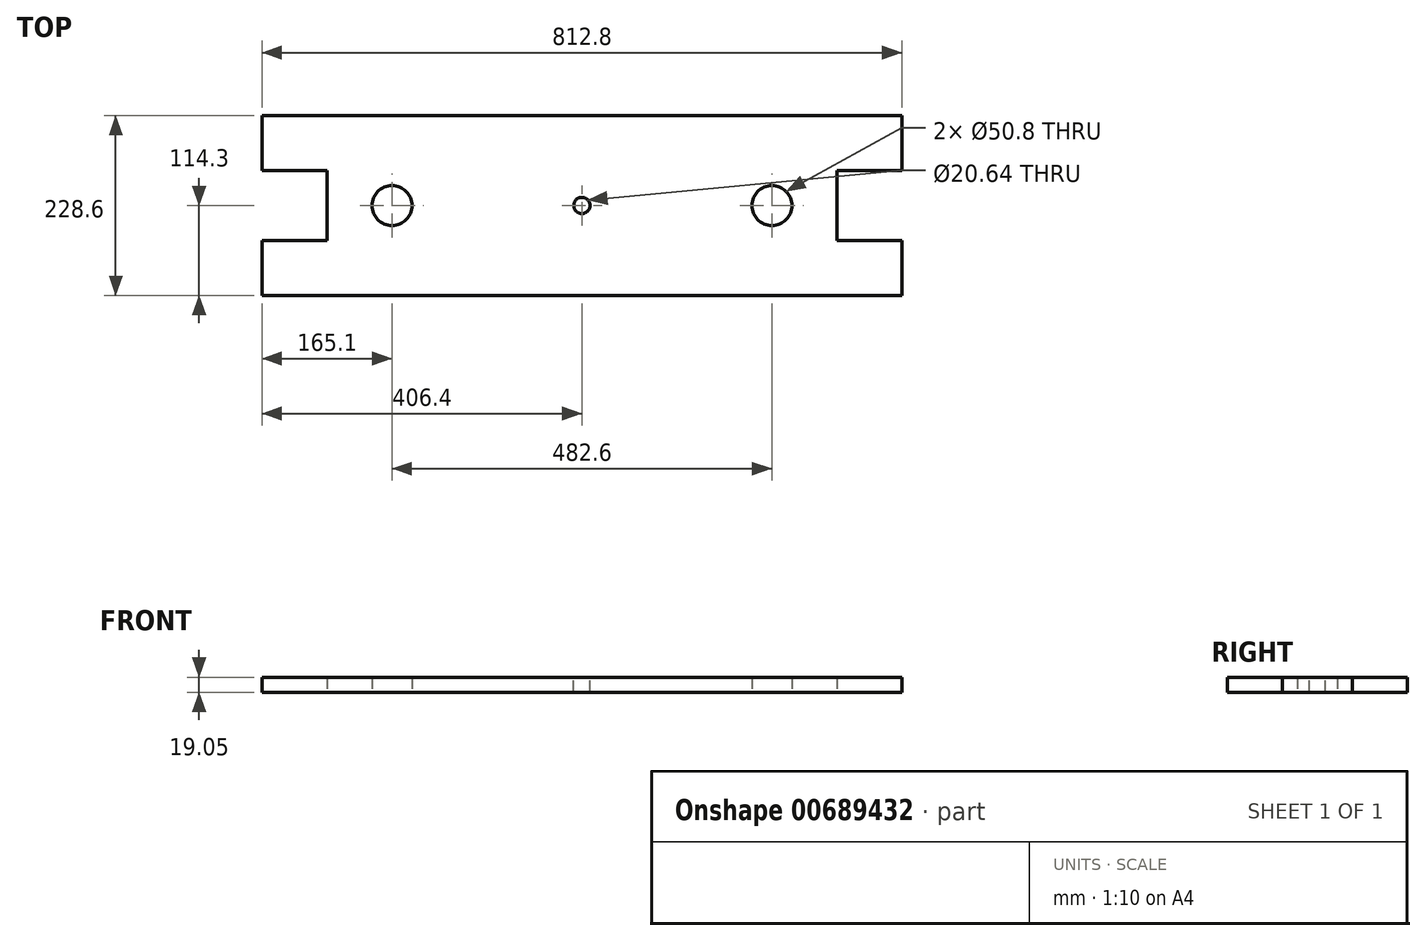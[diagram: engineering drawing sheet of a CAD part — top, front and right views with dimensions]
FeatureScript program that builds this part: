
annotation { "Feature Type Name" : "Feature", "Feature Type Description" : "" }
export const myFeature = defineFeature(function(context is Context, id is Id, definition is map)
    precondition{}
    {
        {
            var Q0;
            Q0=qCreatedBy(makeId("Top.planeOp"),FACE);
            var sketch = newSketch(context, id + "F0", { "sketchPlane" : qUnion([Q0])});
            skLineSegment(sketch, "E0.bottom", {"start": v(-406.4, 114.3) * mm, "end": v(406.4, 114.3) * mm});
            skLineSegment(sketch, "E0.top", {"start": v(-406.4, -114.3) * mm, "end": v(406.4, -114.3) * mm});
            skLineSegment(sketch, "E0.left", {"start": v(-406.4, 114.3) * mm, "end": v(-406.4, 44.45) * mm});
            skLineSegment(sketch, "E0.right", {"start": v(406.4, 114.3) * mm, "end": v(406.4, 44.45) * mm});
            skPoint(sketch, "E0.middle", {"position": v(365.13, 0) * mm});
            skLineSegment(sketch, "E1.bottom", {"start": v(323.85, 44.45) * mm, "end": v(406.4, 44.45) * mm});
            skLineSegment(sketch, "E1.top", {"start": v(323.85, -44.45) * mm, "end": v(406.4, -44.45) * mm});
            skLineSegment(sketch, "E1.left", {"start": v(323.85, 44.45) * mm, "end": v(323.85, -44.45) * mm});
            skLineSegment(sketch, "E2.bottom", {"start": v(-406.4, 44.45) * mm, "end": v(-323.85, 44.45) * mm});
            skLineSegment(sketch, "E2.top", {"start": v(-406.4, -44.45) * mm, "end": v(-323.85, -44.45) * mm});
            skLineSegment(sketch, "E2.left", {"start": v(-406.4, 44.45) * mm, "end": v(-406.4, 44.45) * mm});
            skLineSegment(sketch, "E2.right", {"start": v(-323.85, 44.45) * mm, "end": v(-323.85, -44.45) * mm});
            skPoint(sketch, "E2.middle", {"position": v(-365.13, 0) * mm});
            skLineSegment(sketch, "E3", {"start": v(-406.4, -44.45) * mm, "end": v(-406.4, -114.3) * mm});
            skLineSegment(sketch, "E4", {"start": v(-406.4, -44.45) * mm, "end": v(-406.4, -44.45) * mm});
            skLineSegment(sketch, "E5", {"start": v(406.4, 44.45) * mm, "end": v(406.4, 44.45) * mm});
            skLineSegment(sketch, "E6", {"start": v(406.4, -44.45) * mm, "end": v(406.4, -44.45) * mm});
            skLineSegment(sketch, "E7", {"start": v(406.4, -44.45) * mm, "end": v(406.4, -114.3) * mm});
            skCircle(sketch, "E8", {"center": v(241.3, 0) * mm, "radius": 25.4 * mm});
            skCircle(sketch, "E9", {"center": v(-241.3, 0) * mm, "radius": 25.4 * mm});
            skPoint(sketch, "E10", {"position": v(0, 0) * mm});
            skSolve(sketch);
        }
        {
            var Q0;
            Q0=makeQuery(id+"F0.imprint","IMPRINT",FACE,{"disambiguationData":[TD([[makeQuery(id+"F0.imprint","IMPRINT",EDGE,{"derivedFrom":sQuery(id+"F0.wireOp",EDGE,"E0.bottom")}),-1.0]])]});
            extrude(context, id + "F1", {"entities" : qUnion([Q0]), "depth" : 19.05 * mm, "offsetDistance" : 25.4 * mm});
        }
        {
            var Q0;
            Q0=makeQuery(id+"F1.opExtrude","CAP_FACE",FACE,{"disambiguationData":[OSD([sQuery(id+"F0.wireOp",EDGE,"E0.bottom"),sQuery(id+"F0.wireOp",EDGE,"E0.top"),sQuery(id+"F0.wireOp",EDGE,"E0.left"),sQuery(id+"F0.wireOp",EDGE,"E0.right"),sQuery(id+"F0.wireOp",EDGE,"E1.bottom"),sQuery(id+"F0.wireOp",EDGE,"E1.top"),sQuery(id+"F0.wireOp",EDGE,"E1.left"),sQuery(id+"F0.wireOp",EDGE,"E2.bottom"),sQuery(id+"F0.wireOp",EDGE,"E2.top"),sQuery(id+"F0.wireOp",EDGE,"E2.right"),sQuery(id+"F0.wireOp",EDGE,"E3"),sQuery(id+"F0.wireOp",EDGE,"E7"),sQuery(id+"F0.wireOp",EDGE,"E8"),sQuery(id+"F0.wireOp",EDGE,"E9")])],"isStart":false});
            var sketch = newSketch(context, id + "F2", { "sketchPlane" : qUnion([Q0])});
            skPoint(sketch, "E11", {"position": v(0, 0) * mm});
            skSolve(sketch);
        }
        {
            var Q0;
            Q0=sQuery(id+"F2.wireOp",VERTEX,"E11");
            var Q1;
            Q1=makeQuery(id+"F1.opExtrude","SWEPT_BODY",BODY,{"disambiguationData":[OSD([sQuery(id+"F0.wireOp",EDGE,"E0.bottom"),sQuery(id+"F0.wireOp",EDGE,"E0.top"),sQuery(id+"F0.wireOp",EDGE,"E0.left"),sQuery(id+"F0.wireOp",EDGE,"E0.right"),sQuery(id+"F0.wireOp",EDGE,"E1.bottom"),sQuery(id+"F0.wireOp",EDGE,"E1.top"),sQuery(id+"F0.wireOp",EDGE,"E1.left"),sQuery(id+"F0.wireOp",EDGE,"E2.bottom"),sQuery(id+"F0.wireOp",EDGE,"E2.top"),sQuery(id+"F0.wireOp",EDGE,"E2.right"),sQuery(id+"F0.wireOp",EDGE,"E3"),sQuery(id+"F0.wireOp",EDGE,"E7"),sQuery(id+"F0.wireOp",EDGE,"E8"),sQuery(id+"F0.wireOp",EDGE,"E9")])]});
            hole(context, id + "F3", {"style" : HoleStyle.SIMPLE, "endStyle" : HoleEndStyle.THROUGH, "standardTappedOrClearance" : lookupTablePath({ "standard" : "ANSI", "engagement" : "75%", "pitch" : "14 tpi", "size" : "7/8", "type" : "Tapped" }), "standardBlindInLast" : lookupTablePath({ "standard" : "ANSI", "engagement" : "75%", "pitch" : "14 tpi", "size" : "7/8", "type" : "Tapped" }), "holeDiameter" : 20.64 * mm, "majorDiameter" : 22.22 * mm, "showTappedDepth" : true, "tappedDepth" : 10.3 * mm, "tapClearance" : 3, "locations" : qUnion([Q0]), "scope" : qUnion([Q1])});
        }
    });
